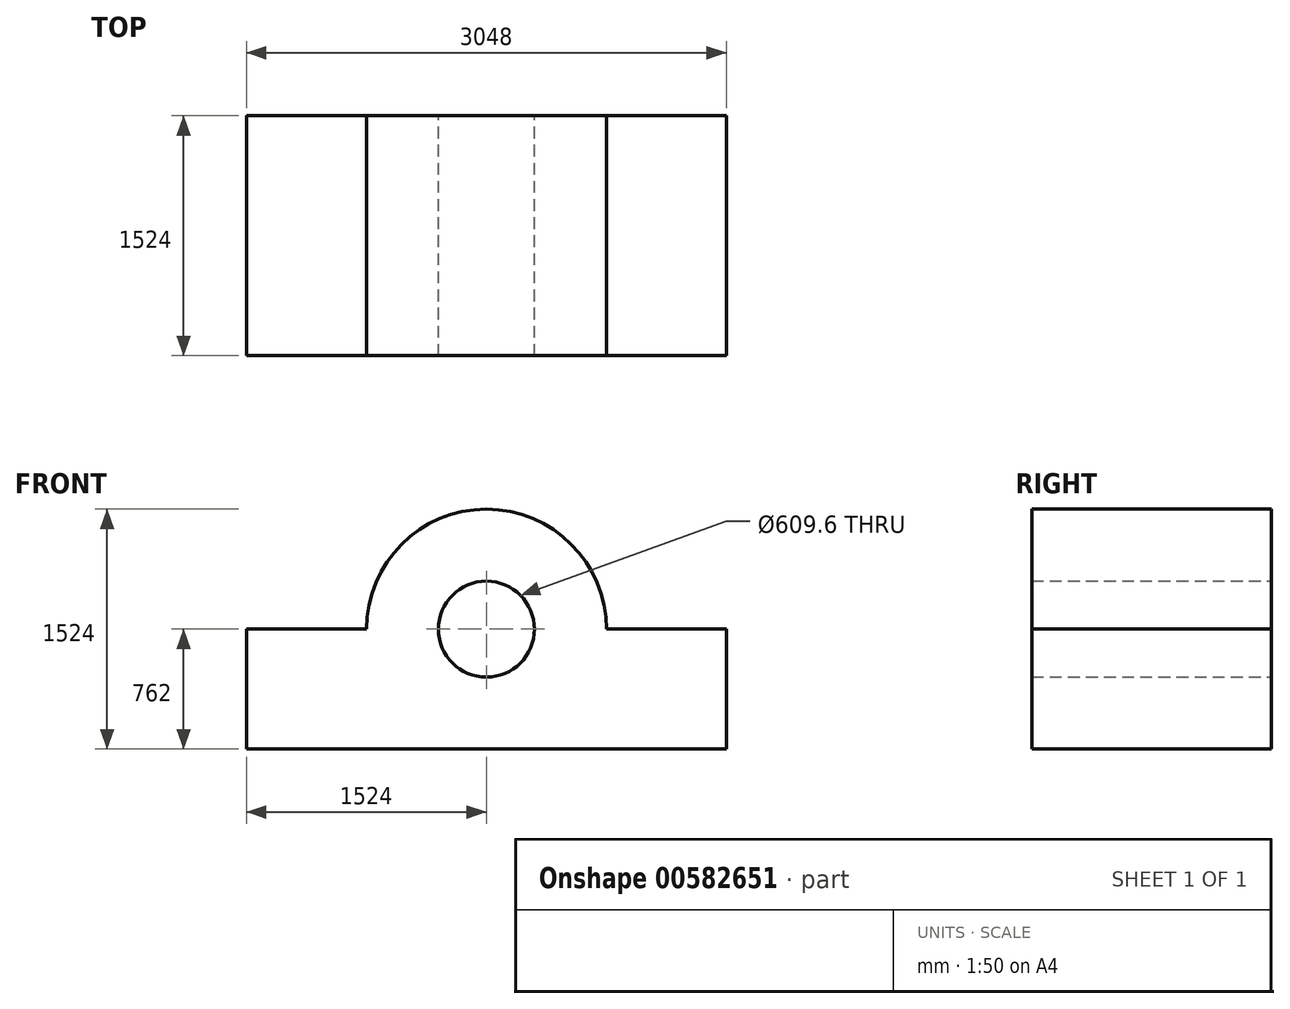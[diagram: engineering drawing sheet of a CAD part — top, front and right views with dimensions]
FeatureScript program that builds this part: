
annotation { "Feature Type Name" : "Feature", "Feature Type Description" : "" }
export const myFeature = defineFeature(function(context is Context, id is Id, definition is map)
    precondition{}
    {
        {
            var Q0;
            Q0=qCreatedBy(makeId("Front.planeOp"),FACE);
            var sketch = newSketch(context, id + "F0", { "sketchPlane" : qUnion([Q0])});
            skLineSegment(sketch, "E0", {"start": v(0, 0) * mm, "end": v(3048, 0) * mm});
            skLineSegment(sketch, "E1", {"start": v(3048, 0) * mm, "end": v(3048, 762) * mm});
            skLineSegment(sketch, "E2", {"start": v(0, 0) * mm, "end": v(0, 762) * mm});
            skPoint(sketch, "E3.orphan", {"position": v(1524, 0) * mm});
            skCircle(sketch, "E4", {"center": v(1524, 762) * mm, "radius": 304.8 * mm});
            skArc(sketch, "E5", {"start": v(2286, 762) * mm, "mid": v(1524, 1524) * mm, "end": v(762, 762) * mm});
            skLineSegment(sketch, "E6", {"start": v(0, 762) * mm, "end": v(762, 762) * mm});
            skLineSegment(sketch, "E7", {"start": v(3048, 762) * mm, "end": v(2286, 762) * mm});
            skSolve(sketch);
        }
        {
            var Q0;
            Q0=makeQuery(id+"F0.imprint","IMPRINT",FACE,{"disambiguationData":[TD([[makeQuery(id+"F0.imprint","IMPRINT",EDGE,{"derivedFrom":sQuery(id+"F0.wireOp",EDGE,"E0")}),1.0]])]});
            extrude(context, id + "F1", {"entities" : qUnion([Q0]), "depth" : 1524 * mm, "offsetDistance" : 25.4 * mm});
        }
    });
